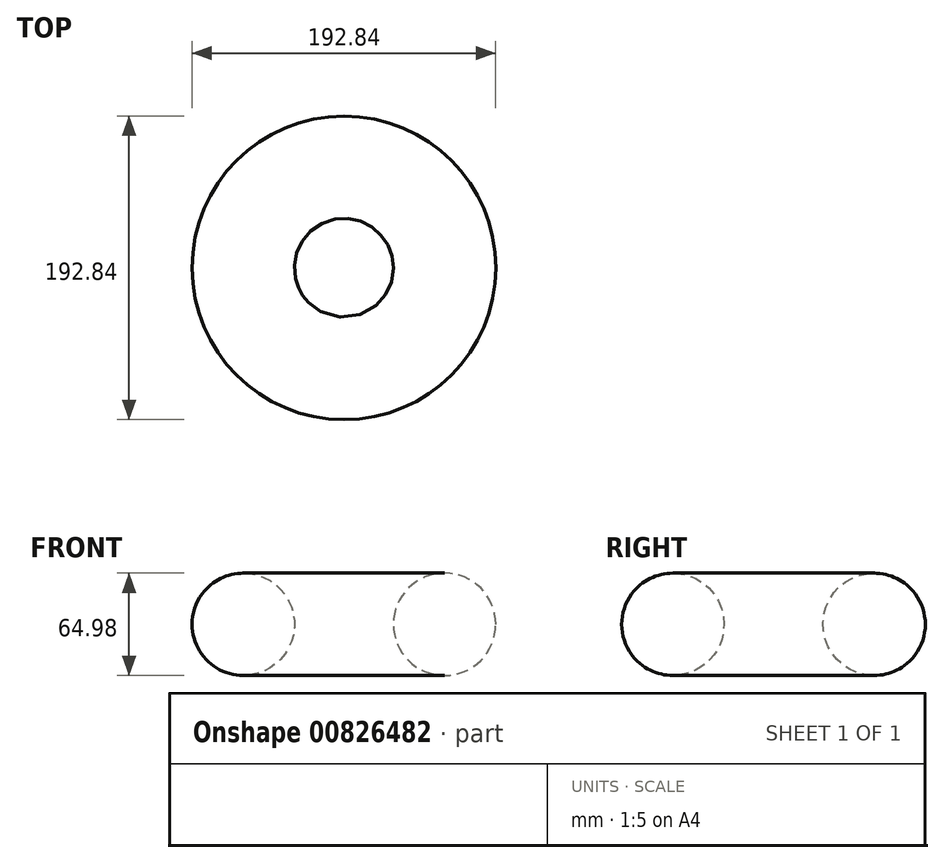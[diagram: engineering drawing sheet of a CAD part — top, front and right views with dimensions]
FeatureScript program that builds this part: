
annotation { "Feature Type Name" : "Feature", "Feature Type Description" : "" }
export const myFeature = defineFeature(function(context is Context, id is Id, definition is map)
    precondition{}
    {
        {
            var Q0;
            Q0=qCreatedBy(makeId("Front.planeOp"),FACE);
            var sketch = newSketch(context, id + "F0", { "sketchPlane" : qUnion([Q0])});
            skCircle(sketch, "E0", {"center": v(-115.02, 31.32) * mm, "radius": 32.49 * mm});
            skLineSegment(sketch, "E1", {"start": v(-51.09, 80.85) * mm, "end": v(-51.09, -24.26) * mm});
            skSolve(sketch);
        }
        {
            var Q0;
            Q0=makeQuery(id+"F0.imprint","IMPRINT",FACE,{"disambiguationData":[TD([[makeQuery(id+"F0.imprint","IMPRINT",EDGE,{"derivedFrom":sQuery(id+"F0.wireOp",EDGE,"E0")}),1.0]])]});
            var Q1;
            Q1=sQuery(id+"F0.wireOp",EDGE,"E1");
            revolve(context, id + "F1", {"surfaceOperationType" : NewSurfaceOperationType.NEW, "entities" : qUnion([Q0]), "axis" : qUnion([Q1]), "revolveType" : RevolveType.FULL});
        }
    });
